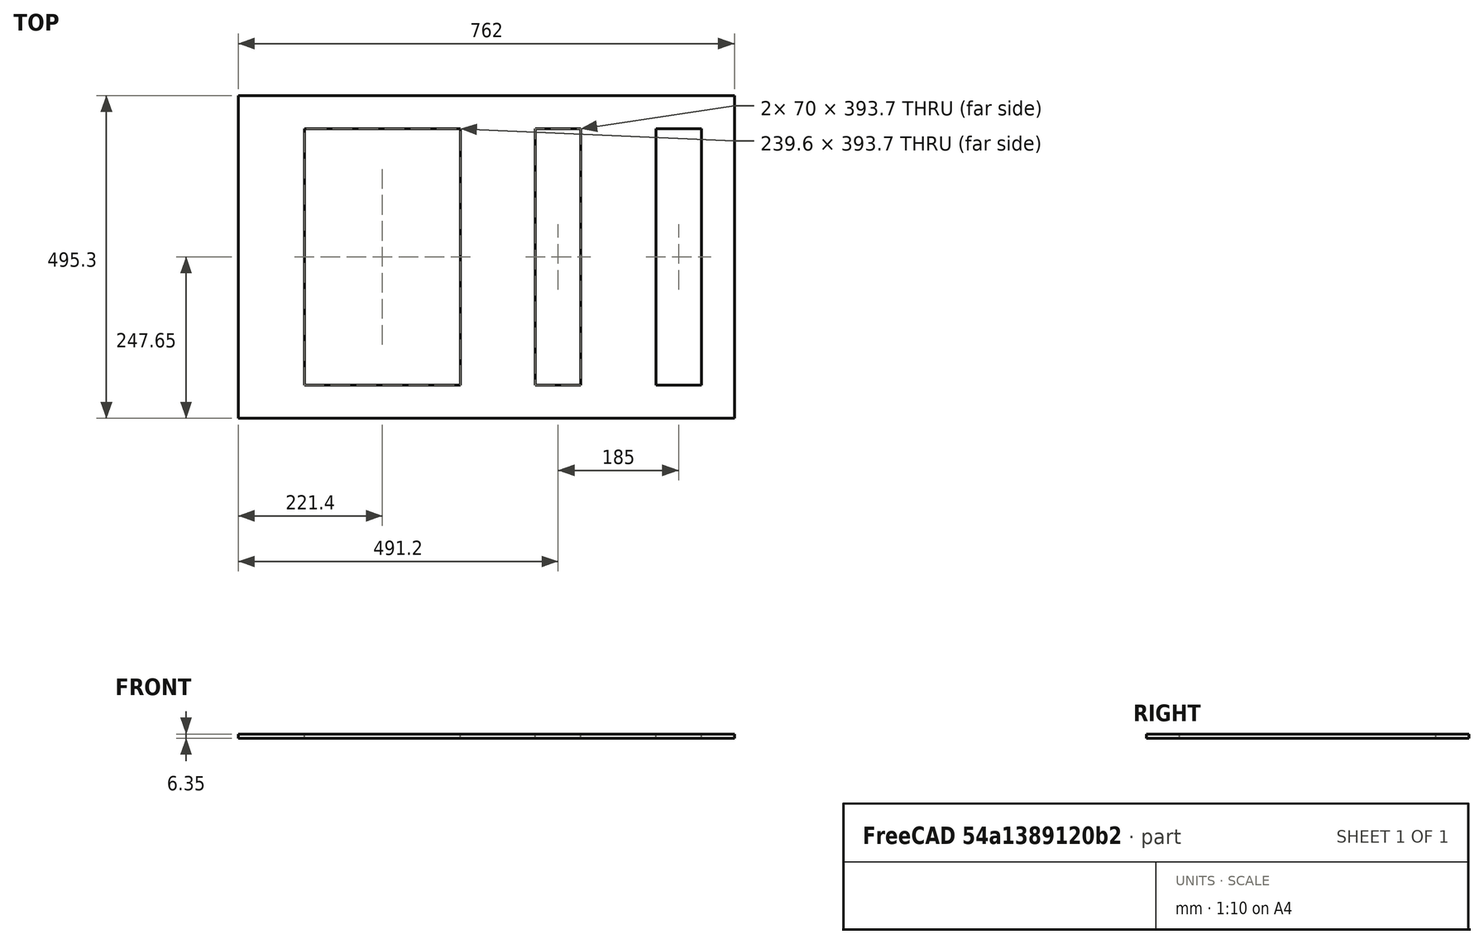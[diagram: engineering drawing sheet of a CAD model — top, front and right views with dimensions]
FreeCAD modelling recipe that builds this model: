
FCSTD DOCUMENT  (FreeCAD 0.16R6712 (Git))
Label: PC_1708_Frame_BOTTOM_side
License: CreativeCommons Attribution
LicenseURL: http://creativecommons.org/licenses/by/4.0/
objects: Sketcher::SketchObject×1, PartDesign::Pad×1
note: 3 computed .brp shape members not serialized (recipe doc carries the construction recipe); baked Part::Feature solids carry a one-line shape summary decoded from their .brp

FEATURE [Sketcher::SketchObject] Sketch
  Placement = pos=(0,0,6.35) rot=(0,0,1;0rad)
  sketch-geometry (16):
    g0: LineSegment StartX=-381 StartY=247.65 StartZ=0 EndX=381 EndY=247.65 EndZ=0
    g1: LineSegment StartX=381 StartY=247.65 StartZ=0 EndX=381 EndY=-247.65 EndZ=0
    g2: LineSegment StartX=381 StartY=-247.65 StartZ=0 EndX=-381 EndY=-247.65 EndZ=0
    g3: LineSegment StartX=-381 StartY=-247.65 StartZ=0 EndX=-381 EndY=247.65 EndZ=0
    g4: LineSegment StartX=330.2 StartY=196.85 StartZ=0 EndX=330.2 EndY=-196.85 EndZ=0
    g5: LineSegment StartX=-279.4 StartY=-196.85 StartZ=0 EndX=-279.4 EndY=196.85 EndZ=0
    g6: LineSegment StartX=330.2 StartY=196.85 StartZ=0 EndX=260.2 EndY=196.85 EndZ=0
    g7: LineSegment StartX=260.2 StartY=196.85 StartZ=0 EndX=260.2 EndY=-196.85 EndZ=0
    g8: LineSegment StartX=260.2 StartY=-196.85 StartZ=0 EndX=330.2 EndY=-196.85 EndZ=0
    g9: LineSegment StartX=145.2 StartY=196.85 StartZ=0 EndX=145.2 EndY=-196.85 EndZ=0
    g10: LineSegment StartX=145.2 StartY=-196.85 StartZ=0 EndX=75.2 EndY=-196.85 EndZ=0
    g11: LineSegment StartX=75.2 StartY=-196.85 StartZ=0 EndX=75.2 EndY=196.85 EndZ=0
    g12: LineSegment StartX=75.2 StartY=196.85 StartZ=0 EndX=145.2 EndY=196.85 EndZ=0
    g13: LineSegment StartX=-39.8 StartY=196.85 StartZ=0 EndX=-39.8 EndY=-196.85 EndZ=0
    g14: LineSegment StartX=-279.4 StartY=196.85 StartZ=0 EndX=-39.8 EndY=196.85 EndZ=0
    g15: LineSegment StartX=-279.4 StartY=-196.85 StartZ=0 EndX=-39.8 EndY=-196.85 EndZ=0
  constraints (48):
    c: Coincident(g0,g1)
    c: Coincident(g1,g2)
    c: Coincident(g2,g3)
    c: Coincident(g3,g0)
    c: Horizontal(g0)
    c: Horizontal(g2)
    c: Vertical(g1)
    c: Vertical(g3)
    c: DistanceX(g0,g0) = 762
    c: Symmetric(g1,g0,g-1)
    c: Symmetric(g0,g0,g-2)
    c: Vertical(g4)
    c: Vertical(g5)
    c: DistanceY(g4,g4) = 393.7
    c: Symmetric(g4,g4,g-1)
    c: DistanceX(g4,g1) = 50.8
    c: DistanceX(g2,g5) = 101.6
    c: DistanceY(g1,g1) = 495.3
    c: Coincident(g4,g6)
    c: Horizontal(g6)
    c: Coincident(g6,g7)
    c: Vertical(g7)
    c: Coincident(g7,g8)
    c: Coincident(g8,g4)
    c: Horizontal(g8)
    c: Vertical(g9)
    c: Coincident(g9,g10)
    c: Horizontal(g10)
    c: Coincident(g10,g11)
    c: Vertical(g11)
    c: Coincident(g11,g12)
    c: Horizontal(g12)
    c: Vertical(g13)
    c: DistanceX(g6,g6) = 70
    c: Coincident(g9,g12)
    c: Distance(g12) = 70
    c: Equal(g7,g9)
    c: Symmetric(g11,g10,g-1)
    c: Distance(g9,g7) = 115
    c: Coincident(g14,g5)
    c: Coincident(g14,g13)
    c: Horizontal(g14)
    c: Coincident(g15,g5)
    c: Horizontal(g15)
    c: Coincident(g13,g15)
    c: Equal(g13,g11)
    c: Symmetric(g13,g13,g-1)
    c: Distance(g13,g10) = 115
FEATURE [PartDesign::Pad] Pad
  Length = 6.35
  Length2 = 100
  Placement = pos=(0,0,6.35) rot=(0,0,1;0rad)
  Sketch = -> Sketch
  Type = 0
